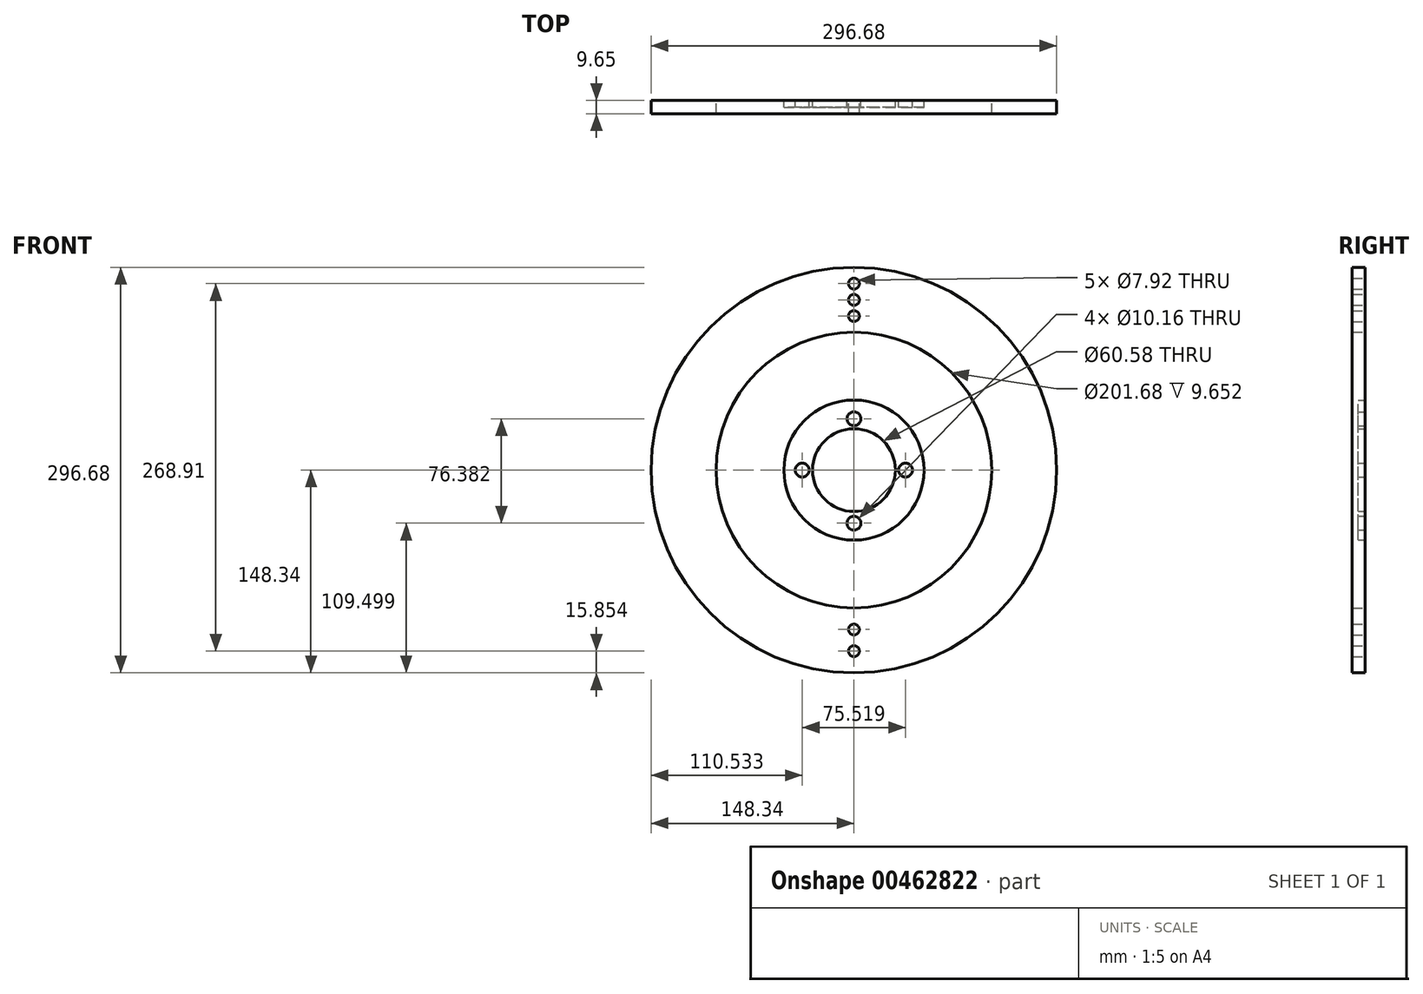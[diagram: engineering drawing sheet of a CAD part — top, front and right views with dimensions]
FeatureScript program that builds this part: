
annotation { "Feature Type Name" : "Feature", "Feature Type Description" : "" }
export const myFeature = defineFeature(function(context is Context, id is Id, definition is map)
    precondition{}
    {
        {
            var Q0;
            Q0=qCreatedBy(makeId("Front.planeOp"),FACE);
            var sketch = newSketch(context, id + "F0", { "sketchPlane" : qUnion([Q0])});
            skCircle(sketch, "E0", {"center": v(0, 0) * mm, "radius": 148.34 * mm});
            skCircle(sketch, "E1", {"center": v(0, 0) * mm, "radius": 100.84 * mm});
            skCircle(sketch, "E2", {"center": v(0, 0) * mm, "radius": 30.29 * mm});
            skCircle(sketch, "E3", {"center": v(0, 0) * mm, "radius": 51.24 * mm});
            skSolve(sketch);
        }
        {
            var Q0;
            Q0=makeQuery(id+"F0.imprint","IMPRINT",FACE,{"disambiguationData":[TD([[makeQuery(id+"F0.imprint","IMPRINT",EDGE,{"derivedFrom":sQuery(id+"F0.wireOp",EDGE,"E1")}),1.0]])]});
            var sketch = newSketch(context, id + "F1", { "sketchPlane" : qUnion([Q0])});
            skPoint(sketch, "E4", {"position": v(0, 37.54) * mm});
            skPoint(sketch, "E5", {"position": v(0, -38.84) * mm});
            skPoint(sketch, "E6", {"position": v(37.71, 0) * mm});
            skPoint(sketch, "E7", {"position": v(-37.8, 0) * mm});
            skSolve(sketch);
        }
        {
            var Q0;
            Q0=makeQuery(id+"F0.imprint","IMPRINT",FACE,{"disambiguationData":[TD([[makeQuery(id+"F0.imprint","IMPRINT",EDGE,{"derivedFrom":sQuery(id+"F0.wireOp",EDGE,"E0")}),1.0]])]});
            var sketch = newSketch(context, id + "F2", { "sketchPlane" : qUnion([Q0])});
            skPoint(sketch, "E8", {"position": v(0, 112.7) * mm});
            skPoint(sketch, "E9", {"position": v(0, 124.56) * mm});
            skPoint(sketch, "E10", {"position": v(0, 136.42) * mm});
            skCircle(sketch, "E11", {"center": v(0, 112.7) * mm, "radius": 3.96 * mm});
            skCircle(sketch, "E12", {"center": v(0, 124.56) * mm, "radius": 3.96 * mm});
            skCircle(sketch, "E13", {"center": v(0, 136.42) * mm, "radius": 3.96 * mm});
            skCircle(sketch, "E14", {"center": v(0, 0) * mm, "radius": 112.7 * mm, "construction": true});
            skCircle(sketch, "E15", {"center": v(0, 0) * mm, "radius": 124.56 * mm, "construction": true});
            skCircle(sketch, "E16", {"center": v(0, 0) * mm, "radius": 136.42 * mm, "construction": true});
            skSolve(sketch);
        }
        {
            var Q0;
            Q0=makeQuery(id+"F0.imprint","IMPRINT",FACE,{"disambiguationData":[TD([[makeQuery(id+"F0.imprint","IMPRINT",EDGE,{"derivedFrom":sQuery(id+"F0.wireOp",EDGE,"E0")}),1.0]])]});
            extrude(context, id + "F3", {"entities" : qUnion([Q0]), "depth" : 9.65 * mm});
        }
        {
            var Q0;
            Q0=qSketchRegion(id+"F2",true);
            extrude(context, id + "F4", {"entities" : qUnion([Q0]), "operationType" : NewBodyOperationType.REMOVE, "endBound" : BoundingType.THROUGH_ALL, "depth" : 25.4 * mm});
        }
        {
            var Q0;
            Q0=makeQuery(id+"F0.imprint","IMPRINT",FACE,{"disambiguationData":[TD([[makeQuery(id+"F0.imprint","IMPRINT",EDGE,{"derivedFrom":sQuery(id+"F0.wireOp",EDGE,"E0")}),1.0]])]});
            var sketch = newSketch(context, id + "F5", { "sketchPlane" : qUnion([Q0])});
            skPoint(sketch, "E17", {"position": v(0, -116.66) * mm});
            skPoint(sketch, "E18", {"position": v(0, -132.49) * mm});
            skSolve(sketch);
        }
        {
            var Q0;
            Q0=sQuery(id+"F5.wireOp",VERTEX,"E17");
            var Q1;
            Q1=sQuery(id+"F5.wireOp",VERTEX,"E18");
            var Q2;
            Q2=makeQuery(id+"F3.opExtrude","SWEPT_BODY",BODY,{"disambiguationData":[OSD([sQuery(id+"F0.wireOp",EDGE,"E0"),sQuery(id+"F0.wireOp",EDGE,"E1")])]});
            hole(context, id + "F6", {"style" : HoleStyle.SIMPLE, "endStyle" : HoleEndStyle.THROUGH, "oppositeDirection" : true, "holeDiameter" : 7.92 * mm, "isTappedThrough" : true, "tappedDepth" : 12.7 * mm, "tapClearance" : 3, "locations" : qUnion([Q0, Q1]), "scope" : qUnion([Q2])});
        }
        {
            var Q0;
            Q0=makeQuery(id+"F0.imprint","IMPRINT",FACE,{"disambiguationData":[TD([[makeQuery(id+"F0.imprint","IMPRINT",EDGE,{"derivedFrom":sQuery(id+"F0.wireOp",EDGE,"E2")}),-1.0]])]});
            extrude(context, id + "F7", {"entities" : qUnion([Q0]), "depth" : 5.08 * mm});
        }
        {
            var Q0;
            Q0=sQuery(id+"F1.wireOp",VERTEX,"E4");
            var Q1;
            Q1=sQuery(id+"F1.wireOp",VERTEX,"E6");
            var Q2;
            Q2=sQuery(id+"F1.wireOp",VERTEX,"E5");
            var Q3;
            Q3=sQuery(id+"F1.wireOp",VERTEX,"E7");
            var Q4;
            Q4=makeQuery(id+"F7.opExtrude","SWEPT_BODY",BODY,{"disambiguationData":[OSD([sQuery(id+"F0.wireOp",EDGE,"E2"),sQuery(id+"F0.wireOp",EDGE,"E3")])]});
            hole(context, id + "F8", {"style" : HoleStyle.SIMPLE, "endStyle" : HoleEndStyle.THROUGH, "oppositeDirection" : true, "holeDiameter" : 10.16 * mm, "isTappedThrough" : true, "tappedDepth" : 12.7 * mm, "tapClearance" : 3, "locations" : qUnion([Q0, Q1, Q2, Q3]), "scope" : qUnion([Q4])});
        }
    });
